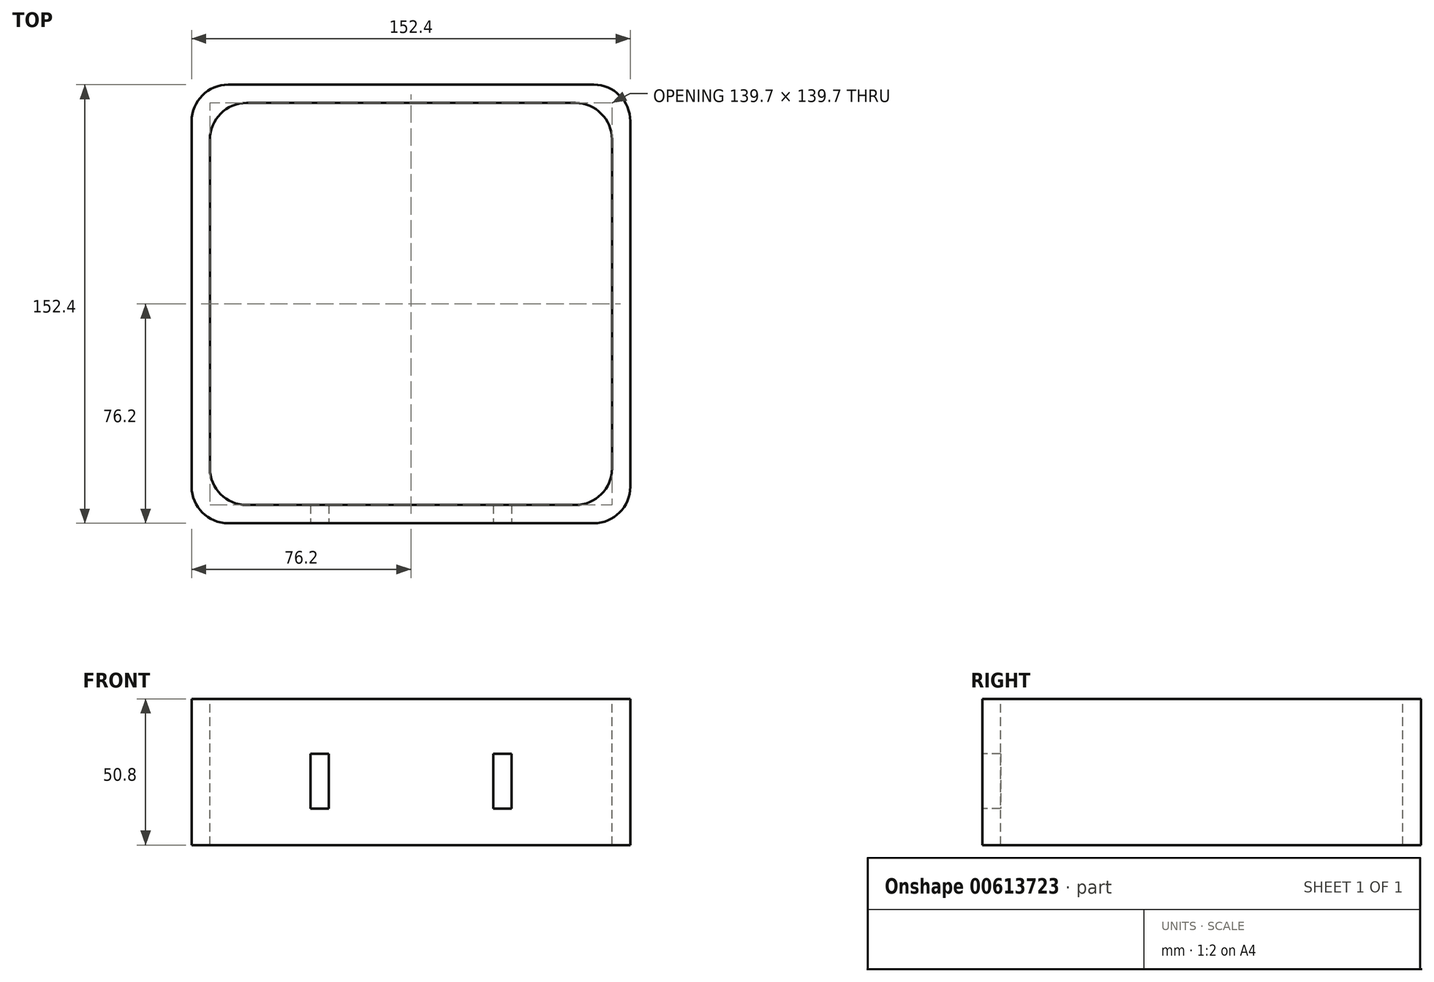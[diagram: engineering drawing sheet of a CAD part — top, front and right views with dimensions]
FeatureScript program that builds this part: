
annotation { "Feature Type Name" : "Feature", "Feature Type Description" : "" }
export const myFeature = defineFeature(function(context is Context, id is Id, definition is map)
    precondition{}
    {
        {
            var Q0;
            Q0=qCreatedBy(makeId("Top.planeOp"),FACE);
            var sketch = newSketch(context, id + "F0", { "sketchPlane" : qUnion([Q0])});
            skLineSegment(sketch, "E0.bottom", {"start": v(-63.5, 76.2) * mm, "end": v(63.5, 76.2) * mm});
            skLineSegment(sketch, "E0.top", {"start": v(-63.5, -76.2) * mm, "end": v(63.5, -76.2) * mm});
            skLineSegment(sketch, "E0.left", {"start": v(-76.2, 63.5) * mm, "end": v(-76.2, -63.5) * mm});
            skLineSegment(sketch, "E0.right", {"start": v(76.2, 63.5) * mm, "end": v(76.2, -63.5) * mm});
            skPoint(sketch, "E1.visualSharp", {"position": v(-76.2, 76.2) * mm});
            skArc(sketch, "E1.filletArc", {"start": v(-63.5, 76.2) * mm, "mid": v(-72.48, 72.48) * mm, "end": v(-76.2, 63.5) * mm});
            skPoint(sketch, "E2.visualSharp", {"position": v(-76.2, -76.2) * mm});
            skArc(sketch, "E2.filletArc", {"start": v(-76.2, -63.5) * mm, "mid": v(-72.48, -72.48) * mm, "end": v(-63.5, -76.2) * mm});
            skPoint(sketch, "E3.visualSharp", {"position": v(76.2, 76.2) * mm});
            skArc(sketch, "E3.filletArc", {"start": v(76.2, 63.5) * mm, "mid": v(72.48, 72.48) * mm, "end": v(63.5, 76.2) * mm});
            skPoint(sketch, "E4.visualSharp", {"position": v(76.2, -76.2) * mm});
            skArc(sketch, "E4.filletArc", {"start": v(63.5, -76.2) * mm, "mid": v(72.48, -72.48) * mm, "end": v(76.2, -63.5) * mm});
            skLineSegment(sketch, "E5.bottom", {"start": v(-57.15, 69.85) * mm, "end": v(57.15, 69.85) * mm});
            skLineSegment(sketch, "E5.top", {"start": v(-57.15, -69.85) * mm, "end": v(57.15, -69.85) * mm});
            skLineSegment(sketch, "E5.left", {"start": v(-69.85, 57.15) * mm, "end": v(-69.85, -57.15) * mm});
            skLineSegment(sketch, "E5.right", {"start": v(69.85, 57.15) * mm, "end": v(69.85, -57.15) * mm});
            skPoint(sketch, "E6.visualSharp", {"position": v(-69.85, 69.85) * mm});
            skArc(sketch, "E6.filletArc", {"start": v(-57.15, 69.85) * mm, "mid": v(-66.13, 66.13) * mm, "end": v(-69.85, 57.15) * mm});
            skPoint(sketch, "E7.visualSharp", {"position": v(-69.85, -69.85) * mm});
            skArc(sketch, "E7.filletArc", {"start": v(-69.85, -57.15) * mm, "mid": v(-66.13, -66.13) * mm, "end": v(-57.15, -69.85) * mm});
            skPoint(sketch, "E8.visualSharp", {"position": v(69.85, 69.85) * mm});
            skArc(sketch, "E8.filletArc", {"start": v(69.85, 57.15) * mm, "mid": v(66.13, 66.13) * mm, "end": v(57.15, 69.85) * mm});
            skPoint(sketch, "E9.visualSharp", {"position": v(69.85, -69.85) * mm});
            skArc(sketch, "E9.filletArc", {"start": v(57.15, -69.85) * mm, "mid": v(66.13, -66.13) * mm, "end": v(69.85, -57.15) * mm});
            skCircle(sketch, "E10", {"center": v(0, 0) * mm, "radius": 69.85 * mm});
            skSolve(sketch);
        }
        {
            var Q0;
            Q0=makeQuery(id+"F0.imprint","IMPRINT",FACE,{"disambiguationData":[TD([[makeQuery(id+"F0.imprint","IMPRINT",EDGE,{"derivedFrom":sQuery(id+"F0.wireOp",EDGE,"E0.bottom")}),-1.0]])]});
            extrude(context, id + "F1", {"entities" : qUnion([Q0]), "oppositeDirection" : true, "depth" : 50.8 * mm, "offsetDistance" : 25.4 * mm});
        }
        {
            var Q0;
            Q0=makeQuery(id+"F1.opExtrude","SWEPT_FACE",FACE,{"disambiguationData":[OSD([sQuery(id+"F0.wireOp",EDGE,"E0.top")])]});
            var sketch = newSketch(context, id + "F2", { "sketchPlane" : qUnion([Q0])});
            skLineSegment(sketch, "E11.bottom", {"start": v(-34.93, -19.05) * mm, "end": v(-28.58, -19.05) * mm});
            skLineSegment(sketch, "E11.top", {"start": v(-34.93, -38.1) * mm, "end": v(-28.58, -38.1) * mm});
            skLineSegment(sketch, "E11.left", {"start": v(-34.93, -19.05) * mm, "end": v(-34.93, -38.1) * mm});
            skLineSegment(sketch, "E11.right", {"start": v(-28.58, -19.05) * mm, "end": v(-28.58, -38.1) * mm});
            skLineSegment(sketch, "E12.bottom", {"start": v(28.57, -19.05) * mm, "end": v(34.92, -19.05) * mm});
            skLineSegment(sketch, "E12.top", {"start": v(28.57, -38.1) * mm, "end": v(34.92, -38.1) * mm});
            skLineSegment(sketch, "E12.left", {"start": v(28.57, -19.05) * mm, "end": v(28.57, -38.1) * mm});
            skLineSegment(sketch, "E12.right", {"start": v(34.92, -19.05) * mm, "end": v(34.92, -38.1) * mm});
            skSolve(sketch);
        }
        {
            var Q0;
            Q0=makeQuery(id+"F2.imprint","IMPRINT",FACE,{"disambiguationData":[TD([[makeQuery(id+"F2.imprint","IMPRINT",EDGE,{"derivedFrom":sQuery(id+"F2.wireOp",EDGE,"E11.bottom")}),-1.0]])]});
            var Q1;
            Q1=makeQuery(id+"F2.imprint","IMPRINT",FACE,{"disambiguationData":[TD([[makeQuery(id+"F2.imprint","IMPRINT",EDGE,{"derivedFrom":sQuery(id+"F2.wireOp",EDGE,"E12.bottom")}),-1.0]])]});
            extrude(context, id + "F3", {"entities" : qUnion([Q0, Q1]), "operationType" : NewBodyOperationType.REMOVE, "oppositeDirection" : true, "depth" : 6.35 * mm, "offsetDistance" : 25.4 * mm});
        }
    });
